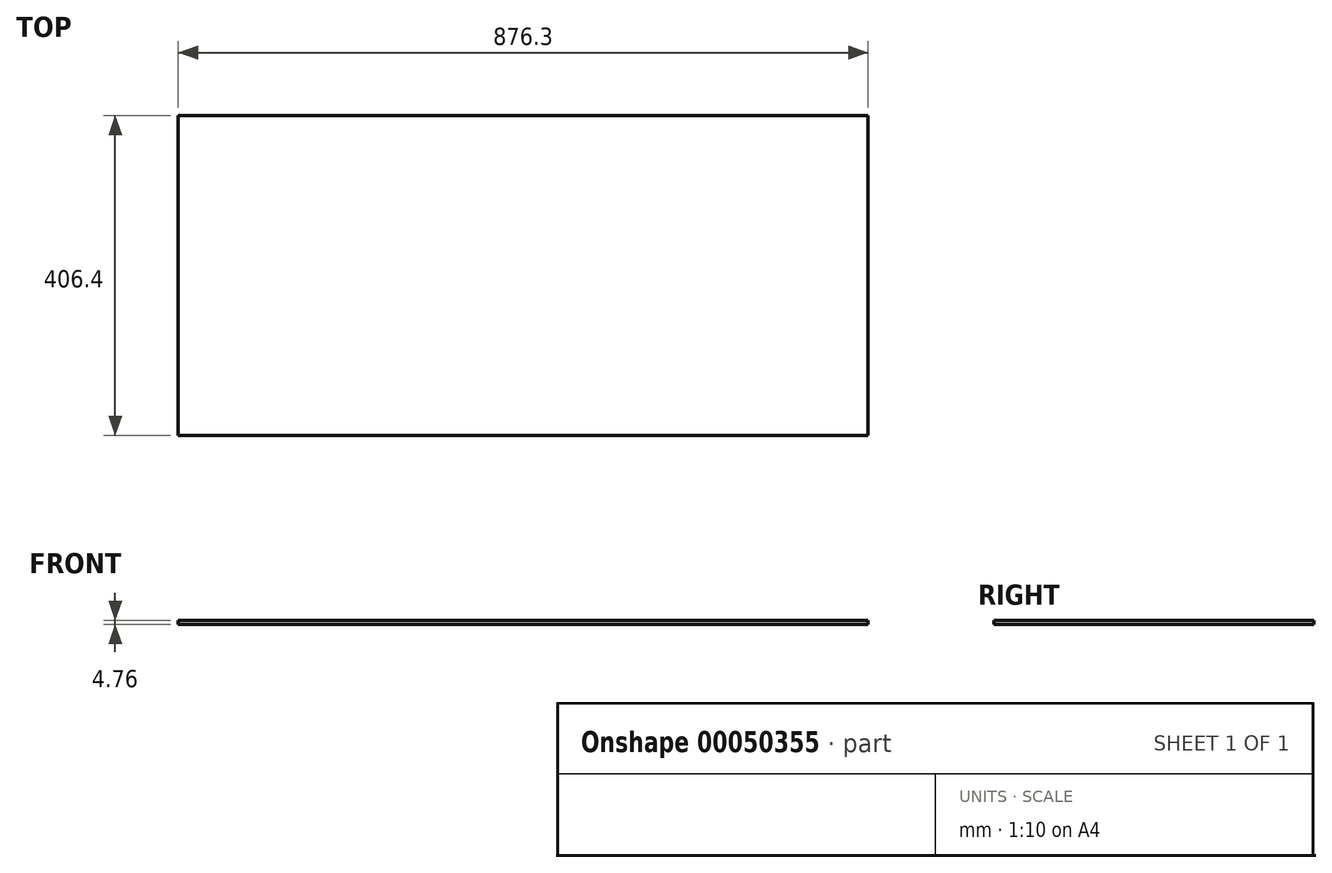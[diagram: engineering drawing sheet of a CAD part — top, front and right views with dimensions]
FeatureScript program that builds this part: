
annotation { "Feature Type Name" : "Feature", "Feature Type Description" : "" }
export const myFeature = defineFeature(function(context is Context, id is Id, definition is map)
    precondition{}
    {
        {
            var Q0;
            Q0=qCreatedBy(makeId("Top.planeOp"),FACE);
            var sketch = newSketch(context, id + "F0", { "sketchPlane" : qUnion([Q0])});
            skLineSegment(sketch, "E0.bottom", {"start": v(-451.55, 158.72) * mm, "end": v(424.75, 158.72) * mm});
            skLineSegment(sketch, "E0.top", {"start": v(-451.55, -247.68) * mm, "end": v(424.75, -247.68) * mm});
            skLineSegment(sketch, "E0.left", {"start": v(-451.55, 158.72) * mm, "end": v(-451.55, -247.68) * mm});
            skLineSegment(sketch, "E0.right", {"start": v(424.75, 158.72) * mm, "end": v(424.75, -247.68) * mm});
            skSolve(sketch);
        }
        {
            var Q0;
            Q0=makeQuery(id+"F0.imprint","IMPRINT",FACE,{"disambiguationData":[TD([[makeQuery(id+"F0.imprint","IMPRINT",EDGE,{"derivedFrom":sQuery(id+"F0.wireOp",EDGE,"E0.bottom")}),-1.0]])]});
            extrude(context, id + "F1", {"entities" : qUnion([Q0]), "depth" : 4.76 * mm});
        }
    });
